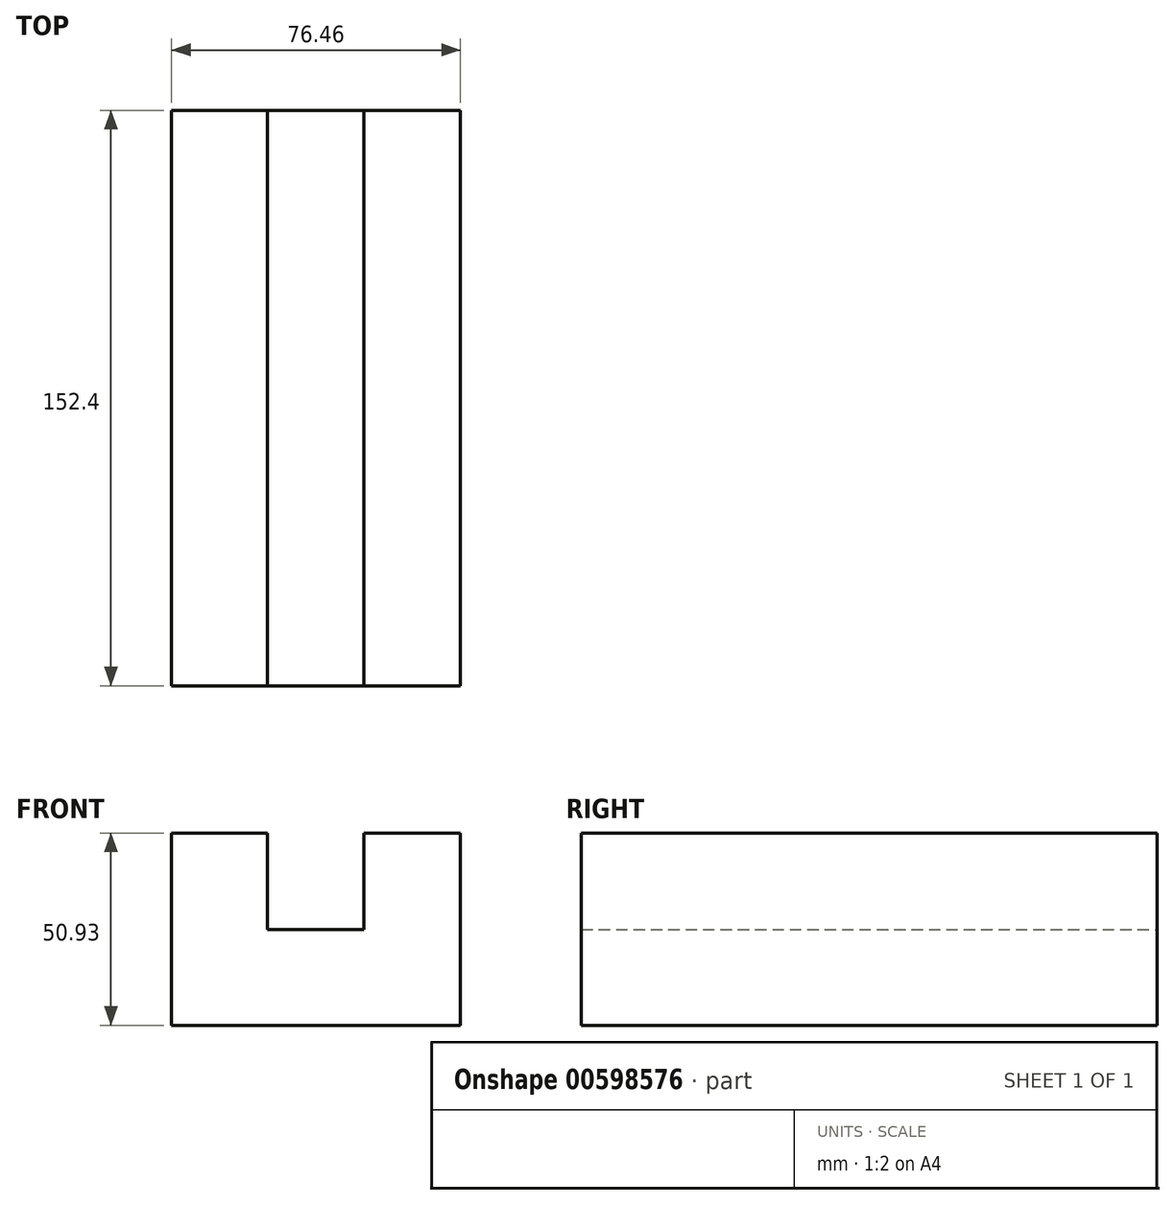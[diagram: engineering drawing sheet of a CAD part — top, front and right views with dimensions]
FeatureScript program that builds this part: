
annotation { "Feature Type Name" : "Feature", "Feature Type Description" : "" }
export const myFeature = defineFeature(function(context is Context, id is Id, definition is map)
    precondition{}
    {
        {
            var Q0;
            Q0=qCreatedBy(makeId("Front.planeOp"),FACE);
            var sketch = newSketch(context, id + "F0", { "sketchPlane" : qUnion([Q0])});
            skLineSegment(sketch, "E0", {"start": v(0, 0) * mm, "end": v(0, 50.93) * mm});
            skLineSegment(sketch, "E1", {"start": v(0, 50.93) * mm, "end": v(25.4, 50.93) * mm});
            skLineSegment(sketch, "E2", {"start": v(25.4, 50.93) * mm, "end": v(25.4, 25.4) * mm});
            skLineSegment(sketch, "E3", {"start": v(25.4, 25.4) * mm, "end": v(50.93, 25.4) * mm});
            skLineSegment(sketch, "E4", {"start": v(50.93, 25.4) * mm, "end": v(50.93, 50.93) * mm});
            skLineSegment(sketch, "E5", {"start": v(50.93, 50.93) * mm, "end": v(76.46, 50.93) * mm});
            skLineSegment(sketch, "E6", {"start": v(76.46, 50.93) * mm, "end": v(76.46, 0) * mm});
            skLineSegment(sketch, "E7", {"start": v(76.46, 0) * mm, "end": v(0, 0) * mm});
            skSolve(sketch);
        }
        {
            var Q0;
            Q0 = qSketchRegion(id + "F0", true);
            extrude(context, id + "F1", {"entities" : qUnion([Q0]), "depth" : 152.4 * mm, "offsetDistance" : 25.4 * mm});
        }
    });
